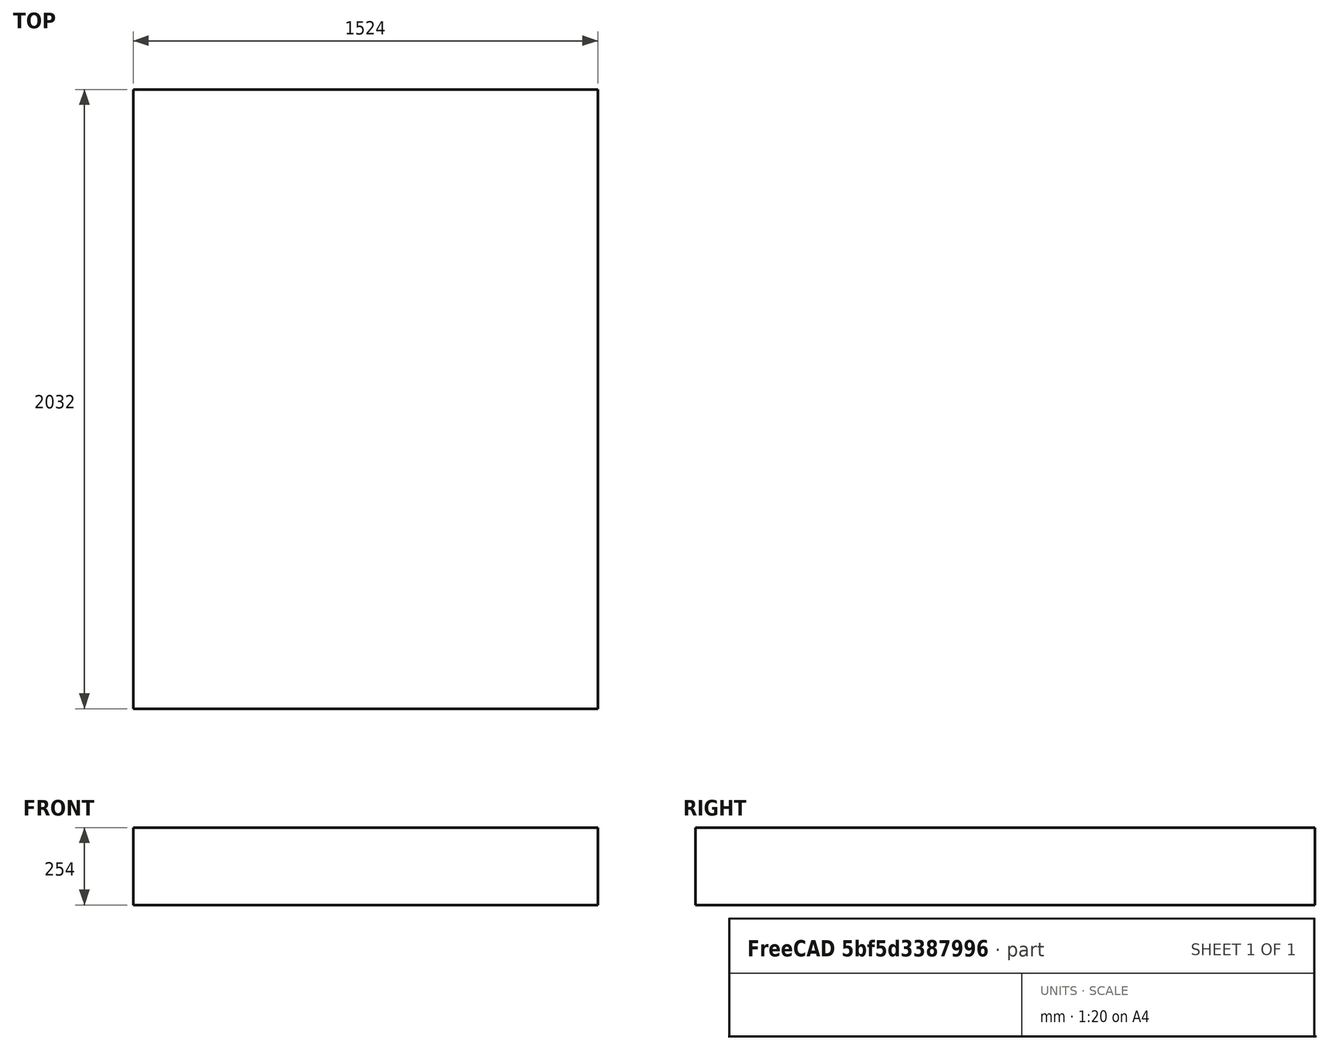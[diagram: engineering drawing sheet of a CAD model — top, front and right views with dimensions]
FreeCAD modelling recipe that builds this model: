
FCSTD DOCUMENT  (FreeCAD 0.18.3R)
Label: queen_mattress
License: All rights reserved
LicenseURL: http://en.wikipedia.org/wiki/All_rights_reserved
objects: Sketcher::SketchObject×1, PartDesign::Pad×1, PartDesign::Body×1
note: 4 computed .brp shape members not serialized (recipe doc carries the construction recipe); baked Part::Feature solids carry a one-line shape summary decoded from their .brp

FEATURE [Sketcher::SketchObject] Sketch
  MapMode = 5
  Support = -> [XY_Plane]
  sketch-geometry (4):
    g0: LineSegment StartX=0 StartY=-2032 StartZ=0 EndX=-1524 EndY=-2032 EndZ=0
    g1: LineSegment StartX=-1524 StartY=-2032 StartZ=0 EndX=-1524 EndY=0 EndZ=0
    g2: LineSegment StartX=-1524 StartY=0 StartZ=0 EndX=0 EndY=0 EndZ=0
    g3: LineSegment StartX=0 StartY=0 StartZ=0 EndX=0 EndY=-2032 EndZ=0
  constraints (11):
    c: Coincident(g0,g1)
    c: Coincident(g1,g2)
    c: Coincident(g2,g3)
    c: Coincident(g3,g0)
    c: Horizontal(g0)
    c: Horizontal(g2)
    c: Vertical(g1)
    c: Vertical(g3)
    c: DistanceX(g2,g2) = 1524
    c: DistanceY(g3,g3) = 2032
    c: Coincident(g2,g-1)
FEATURE [PartDesign::Pad] Pad
  Length = 254
  Length2 = 100
  Profile = -> Sketch
  Type = 0
FEATURE [PartDesign::Body] Body
  Group = -> [Sketch,Pad]
  Origin = -> Origin
  Tip = -> Pad
